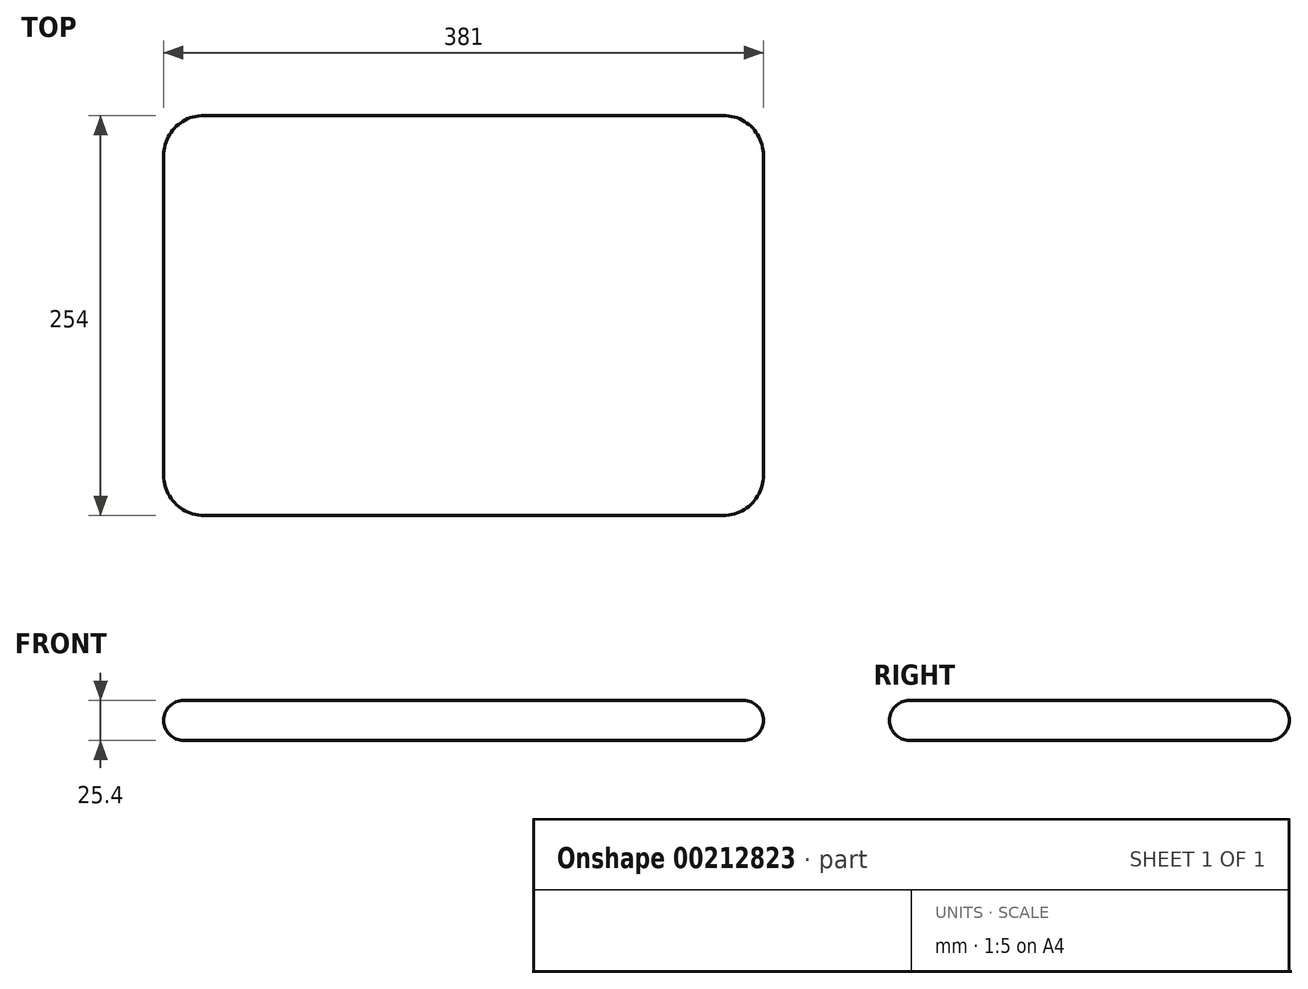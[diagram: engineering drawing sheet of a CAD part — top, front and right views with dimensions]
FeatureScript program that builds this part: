
annotation { "Feature Type Name" : "Feature", "Feature Type Description" : "" }
export const myFeature = defineFeature(function(context is Context, id is Id, definition is map)
    precondition{}
    {
        {
            var Q0;
            Q0=qCreatedBy(makeId("Top.planeOp"),FACE);
            var sketch = newSketch(context, id + "F0", { "sketchPlane" : qUnion([Q0])});
            skLineSegment(sketch, "E0.bottom", {"start": v(-165.1, 127) * mm, "end": v(165.1, 127) * mm});
            skLineSegment(sketch, "E0.top", {"start": v(-165.1, -127) * mm, "end": v(165.1, -127) * mm});
            skLineSegment(sketch, "E0.left", {"start": v(-190.5, 101.6) * mm, "end": v(-190.5, -101.6) * mm});
            skLineSegment(sketch, "E0.right", {"start": v(190.5, 101.6) * mm, "end": v(190.5, -101.6) * mm});
            skPoint(sketch, "E0.middle", {"position": v(0, 0) * mm});
            skPoint(sketch, "E1.visualSharp", {"position": v(-190.5, 127) * mm});
            skArc(sketch, "E1.filletArc", {"start": v(-165.1, 127) * mm, "mid": v(-183.06, 119.56) * mm, "end": v(-190.5, 101.6) * mm});
            skPoint(sketch, "E2.visualSharp", {"position": v(-190.5, -127) * mm});
            skArc(sketch, "E2.filletArc", {"start": v(-190.5, -101.6) * mm, "mid": v(-183.06, -119.56) * mm, "end": v(-165.1, -127) * mm});
            skPoint(sketch, "E3.visualSharp", {"position": v(190.5, -127) * mm});
            skArc(sketch, "E3.filletArc", {"start": v(165.1, -127) * mm, "mid": v(183.06, -119.56) * mm, "end": v(190.5, -101.6) * mm});
            skPoint(sketch, "E4.visualSharp", {"position": v(190.5, 127) * mm});
            skArc(sketch, "E4.filletArc", {"start": v(190.5, 101.6) * mm, "mid": v(183.06, 119.56) * mm, "end": v(165.1, 127) * mm});
            skSolve(sketch);
        }
        {
            var Q0;
            Q0=makeQuery(id+"F0.imprint","IMPRINT",FACE,{"disambiguationData":[TD([[makeQuery(id+"F0.imprint","IMPRINT",EDGE,{"derivedFrom":sQuery(id+"F0.wireOp",EDGE,"E0.bottom")}),-1.0]])]});
            extrude(context, id + "F1", {"entities" : qUnion([Q0]), "endBound" : BoundingType.SYMMETRIC, "depth" : 25.4 * mm});
        }
        {
            var Q0;
            Q0=makeQuery(id+"F1.opExtrude","CAP_FACE",FACE,{"disambiguationData":[OSD([sQuery(id+"F0.wireOp",EDGE,"E0.bottom"),sQuery(id+"F0.wireOp",EDGE,"E0.top"),sQuery(id+"F0.wireOp",EDGE,"E0.left"),sQuery(id+"F0.wireOp",EDGE,"E0.right"),sQuery(id+"F0.wireOp",EDGE,"E1.filletArc"),sQuery(id+"F0.wireOp",EDGE,"E2.filletArc"),sQuery(id+"F0.wireOp",EDGE,"E3.filletArc"),sQuery(id+"F0.wireOp",EDGE,"E4.filletArc")])],"isStart":false});
            var Q1;
            Q1=makeQuery(id+"F1.opExtrude","CAP_FACE",FACE,{"disambiguationData":[OSD([sQuery(id+"F0.wireOp",EDGE,"E0.bottom"),sQuery(id+"F0.wireOp",EDGE,"E0.top"),sQuery(id+"F0.wireOp",EDGE,"E0.left"),sQuery(id+"F0.wireOp",EDGE,"E0.right"),sQuery(id+"F0.wireOp",EDGE,"E1.filletArc"),sQuery(id+"F0.wireOp",EDGE,"E2.filletArc"),sQuery(id+"F0.wireOp",EDGE,"E3.filletArc"),sQuery(id+"F0.wireOp",EDGE,"E4.filletArc")])],"isStart":true});
            fillet(context, id + "F2", {"entities" : qUnion([Q0, Q1]), "radius" : 12.7 * mm, "tangentPropagation" : true, "allowEdgeOverflow" : false});
        }
    });
